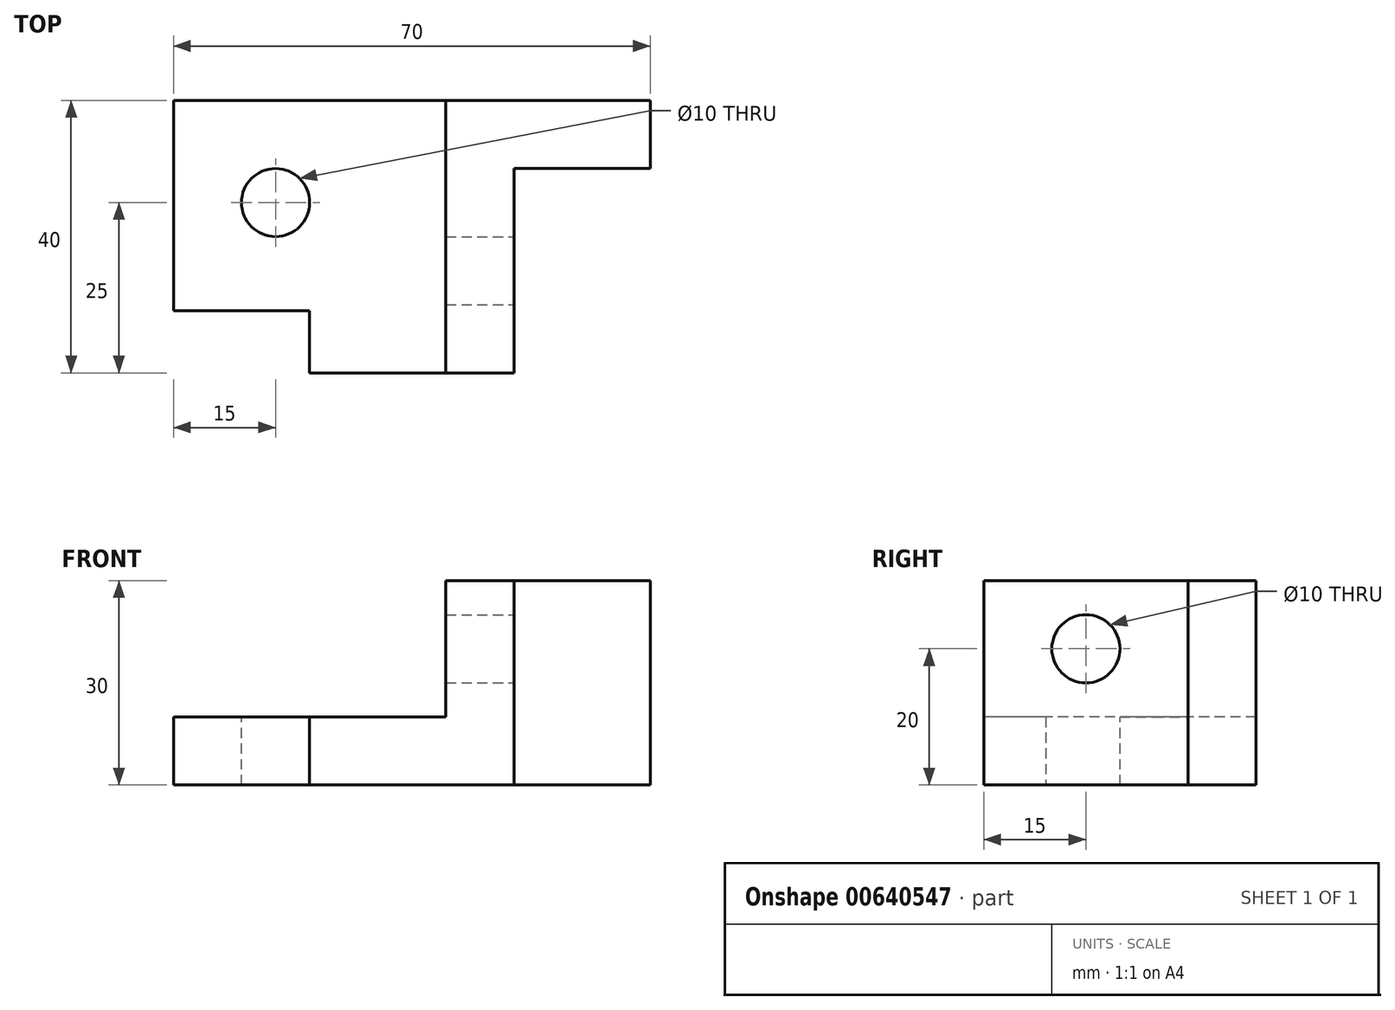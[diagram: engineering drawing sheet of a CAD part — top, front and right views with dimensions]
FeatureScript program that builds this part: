
annotation { "Feature Type Name" : "Feature", "Feature Type Description" : "" }
export const myFeature = defineFeature(function(context is Context, id is Id, definition is map)
    precondition{}
    {
        {
            var Q0;
            Q0=qCreatedBy(makeId("Top.planeOp"),FACE);
            var sketch = newSketch(context, id + "F0", { "sketchPlane" : qUnion([Q0])});
            skLineSegment(sketch, "E0.bottom", {"start": v(35, 20) * mm, "end": v(-35, 20) * mm});
            skLineSegment(sketch, "E0.top", {"start": v(15, -20) * mm, "end": v(-15, -20) * mm});
            skLineSegment(sketch, "E0.left", {"start": v(35, 20) * mm, "end": v(35, 10) * mm});
            skLineSegment(sketch, "E0.right", {"start": v(-35, 20) * mm, "end": v(-35, -10.88) * mm});
            skPoint(sketch, "E0.middle", {"position": v(0, 0) * mm});
            skLineSegment(sketch, "E1.bottom", {"start": v(-35, -10.88) * mm, "end": v(-15, -10.88) * mm});
            skLineSegment(sketch, "E1.right", {"start": v(-15, -10.88) * mm, "end": v(-15, -20) * mm});
            skLineSegment(sketch, "E2.top", {"start": v(15, 10) * mm, "end": v(35, 10) * mm});
            skLineSegment(sketch, "E2.left", {"start": v(15, -20) * mm, "end": v(15, 10) * mm});
            skPoint(sketch, "E3.orphan", {"position": v(-35, -20) * mm});
            skPoint(sketch, "E4.orphan", {"position": v(35, -20) * mm});
            skLineSegment(sketch, "E5.bottom", {"start": v(15, -20) * mm, "end": v(5, -20) * mm});
            skLineSegment(sketch, "E5.top", {"start": v(15, 20) * mm, "end": v(5, 20) * mm});
            skLineSegment(sketch, "E5.right", {"start": v(5, -20) * mm, "end": v(5, 20) * mm});
            skSolve(sketch);
        }
        {
            var Q0;
            Q0=makeQuery(id+"F0.imprint","IMPRINT",FACE,{"disambiguationData":[TD([[makeQuery(id+"F0.imprint","IMPRINT",EDGE,{"derivedFrom":sQuery(id+"F0.wireOp",EDGE,"E0.top")}),-1.0]])]});
            extrude(context, id + "F1", {"entities" : qUnion([Q0]), "depth" : 10 * mm, "offsetDistance" : 25 * mm});
        }
        {
            var Q0;
            {var subQ0=sQuery(id+"F0.wireOp",EDGE,"E0.left");Q0=makeQuery(id+"F0.imprint","IMPRINT",FACE,{"disambiguationData":[TD([[makeQuery(id+"F0.imprint","IMPRINT",EDGE,{"derivedFrom":subQ0}),-1.0]])]});}
            extrude(context, id + "F2", {"entities" : qUnion([Q0]), "operationType" : NewBodyOperationType.ADD, "depth" : 30 * mm, "offsetDistance" : 25 * mm});
        }
        {
            var Q0;
            Q0=makeQuery(id+"F2.opExtrude","SWEPT_FACE",FACE,{"disambiguationData":[OSD([sQuery(id+"F0.wireOp",EDGE,"E2.left")])]});
            var sketch = newSketch(context, id + "F3", { "sketchPlane" : qUnion([Q0])});
            skCircle(sketch, "E6", {"center": v(-5, 20) * mm, "radius": 5 * mm});
            skSolve(sketch);
        }
        {
            var Q0;
            Q0=makeQuery(id+"F3.imprint","IMPRINT",FACE,{"disambiguationData":[TD([[makeQuery(id+"F3.imprint","IMPRINT",EDGE,{"derivedFrom":sQuery(id+"F3.wireOp",EDGE,"E6")}),1.0]])]});
            extrude(context, id + "F4", {"entities" : qUnion([Q0]), "operationType" : NewBodyOperationType.REMOVE, "oppositeDirection" : true, "depth" : 25 * mm, "offsetDistance" : 25 * mm});
        }
        {
            var Q0;
            Q0=makeQuery(id+"F1.opExtrude","CAP_FACE",FACE,{"disambiguationData":[OSD([sQuery(id+"F0.wireOp",EDGE,"E0.bottom"),sQuery(id+"F0.wireOp",EDGE,"E0.top"),sQuery(id+"F0.wireOp",EDGE,"E0.right"),sQuery(id+"F0.wireOp",EDGE,"E1.bottom"),sQuery(id+"F0.wireOp",EDGE,"E1.right"),sQuery(id+"F0.wireOp",EDGE,"E5.right")])],"isStart":false});
            var sketch = newSketch(context, id + "F5", { "sketchPlane" : qUnion([Q0])});
            skCircle(sketch, "E7", {"center": v(-20, 5) * mm, "radius": 5 * mm});
            skSolve(sketch);
        }
        {
            var Q0;
            Q0=makeQuery(id+"F5.imprint","IMPRINT",FACE,{"disambiguationData":[TD([[makeQuery(id+"F5.imprint","IMPRINT",EDGE,{"derivedFrom":sQuery(id+"F5.wireOp",EDGE,"E7")}),1.0]])]});
            extrude(context, id + "F6", {"entities" : qUnion([Q0]), "operationType" : NewBodyOperationType.REMOVE, "oppositeDirection" : true, "depth" : 25 * mm, "offsetDistance" : 25 * mm});
        }
    });
